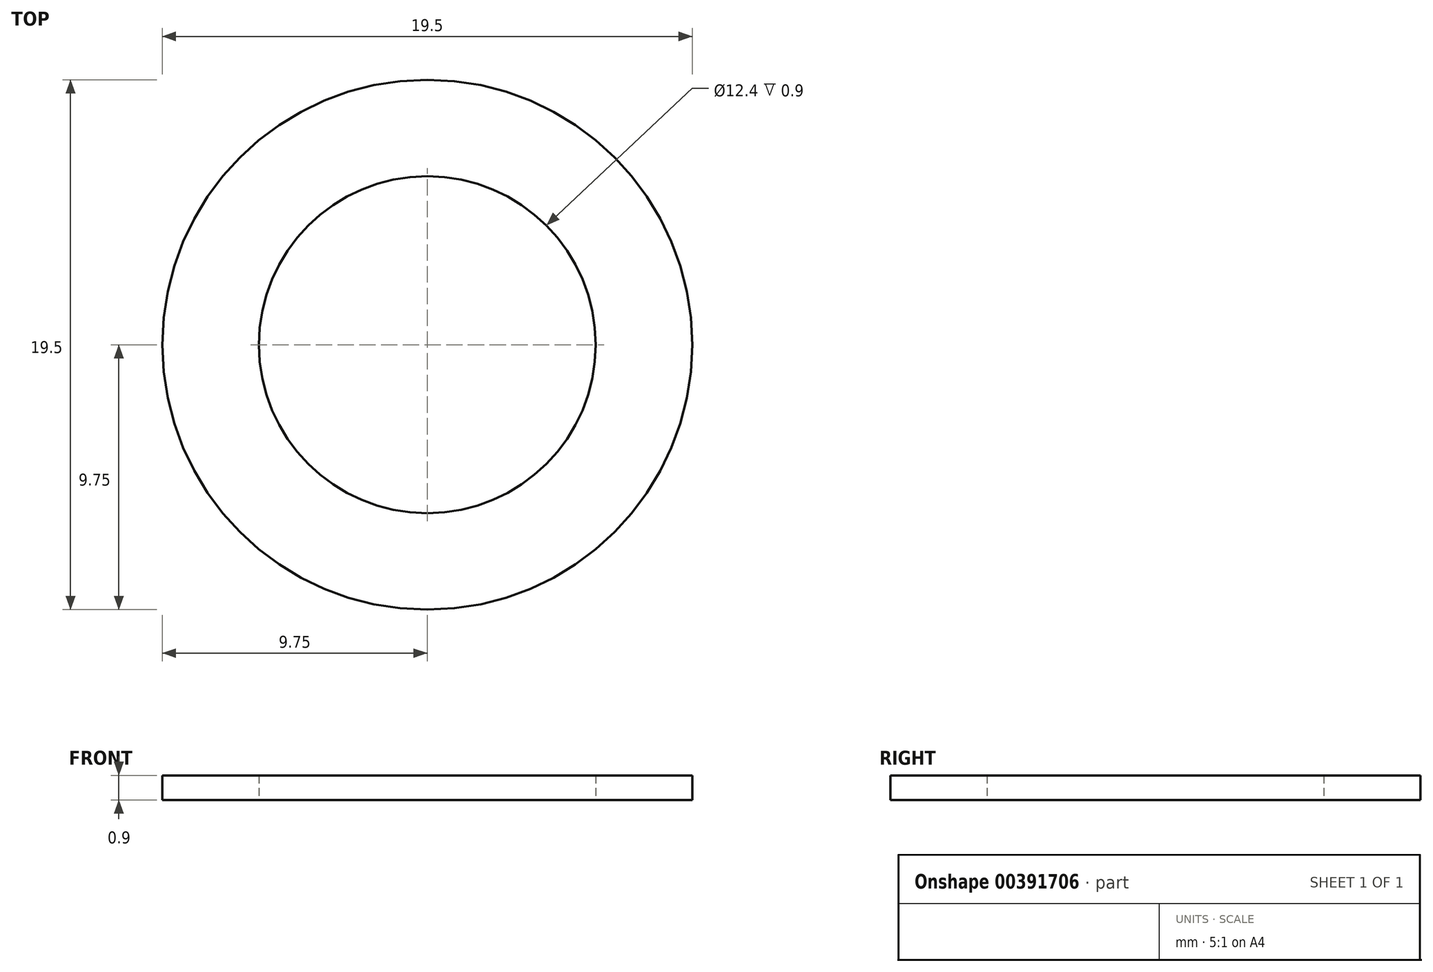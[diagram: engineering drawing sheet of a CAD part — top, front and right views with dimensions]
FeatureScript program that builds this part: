
annotation { "Feature Type Name" : "Feature", "Feature Type Description" : "" }
export const myFeature = defineFeature(function(context is Context, id is Id, definition is map)
    precondition{}
    {
        {
            var Q0;
            Q0=qCreatedBy(makeId("Top.planeOp"),FACE);
            var sketch = newSketch(context, id + "F0", { "sketchPlane" : qUnion([Q0])});
            skCircle(sketch, "E0", {"center": v(0, 0) * mm, "radius": 9.75 * mm});
            skCircle(sketch, "E1", {"center": v(0, 0) * mm, "radius": 6.2 * mm});
            skSolve(sketch);
        }
        {
            var Q0;
            Q0 = qSketchRegion(id + "F0", true);
            extrude(context, id + "F1", {"entities" : qUnion([Q0]), "depth" : 0.9 * mm});
        }
    });
